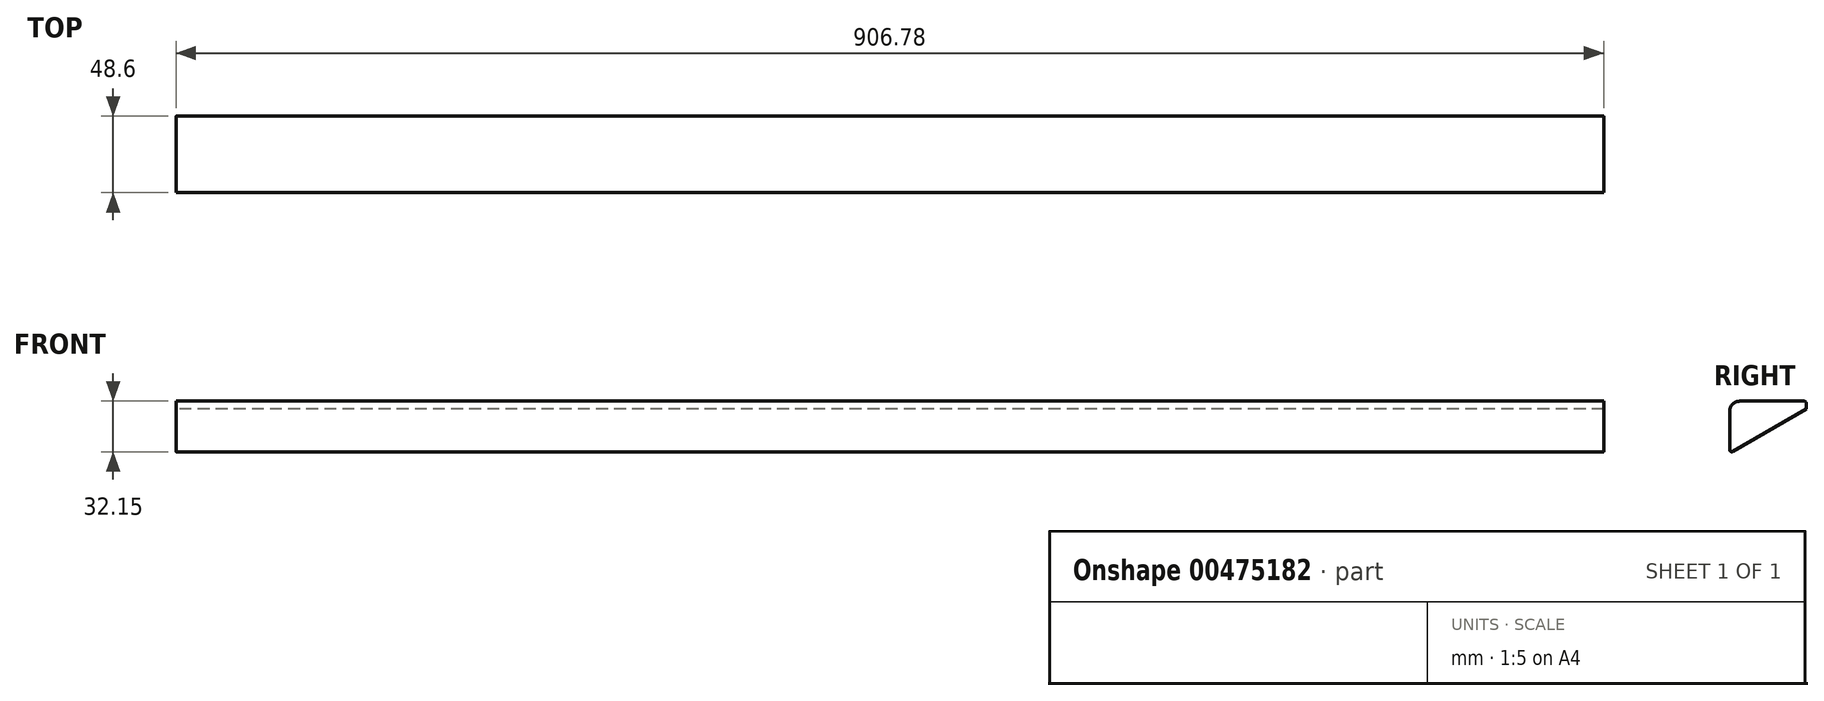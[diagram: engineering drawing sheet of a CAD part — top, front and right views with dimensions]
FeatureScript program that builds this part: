
annotation { "Feature Type Name" : "Feature", "Feature Type Description" : "" }
export const myFeature = defineFeature(function(context is Context, id is Id, definition is map)
    precondition{}
    {
        {
            var Q0;
            Q0=qCreatedBy(makeId("Right.planeOp"),FACE);
            var sketch = newSketch(context, id + "F0", { "sketchPlane" : qUnion([Q0])});
            skLineSegment(sketch, "E0.bottom", {"start": v(24.3, 19.05) * mm, "end": v(-17.95, 19.05) * mm});
            skLineSegment(sketch, "E0.left", {"start": v(24.3, 19.05) * mm, "end": v(24.3, 14.02) * mm});
            skLineSegment(sketch, "E0.right", {"start": v(-24.3, 12.7) * mm, "end": v(-24.3, -14.03) * mm});
            skPoint(sketch, "E0.middle", {"position": v(0, 0) * mm});
            skLineSegment(sketch, "E1", {"start": v(-24.3, -14.03) * mm, "end": v(24.3, 14.02) * mm});
            skPoint(sketch, "E2.orphan", {"position": v(-24.3, -19.05) * mm});
            skPoint(sketch, "E3.orphan", {"position": v(24.3, -19.05) * mm});
            skPoint(sketch, "E4.visualSharp", {"position": v(-24.3, 19.05) * mm});
            skArc(sketch, "E4.filletArc", {"start": v(-17.95, 19.05) * mm, "mid": v(-22.44, 17.2) * mm, "end": v(-24.3, 12.7) * mm});
            skSolve(sketch);
        }
        {
            var Q0;
            Q0=makeQuery(id+"F0.imprint","IMPRINT",FACE,{"disambiguationData":[TD([[makeQuery(id+"F0.imprint","IMPRINT",EDGE,{"derivedFrom":sQuery(id+"F0.wireOp",EDGE,"E0.bottom")}),1.0]])]});
            extrude(context, id + "F1", {"entities" : qUnion([Q0]), "depth" : 906.78 * mm});
        }
        {
            var Q0;
            Q0=makeQuery(id+"F1.opExtrude","SWEPT_EDGE",EDGE,{"disambiguationData":[OSD([sQuery(id+"F0.wireOp",EDGE,"E0.right"),sQuery(id+"F0.wireOp",EDGE,"E1")])]});
            var Q1;
            Q1=makeQuery(id+"F1.opExtrude","SWEPT_EDGE",EDGE,{"disambiguationData":[OSD([sQuery(id+"F0.wireOp",EDGE,"E0.bottom"),sQuery(id+"F0.wireOp",EDGE,"E0.left")])]});
            fillet(context, id + "F2", {"entities" : qUnion([Q0, Q1]), "radius" : 1.27 * mm, "tangentPropagation" : true, "allowEdgeOverflow" : false});
        }
    });
